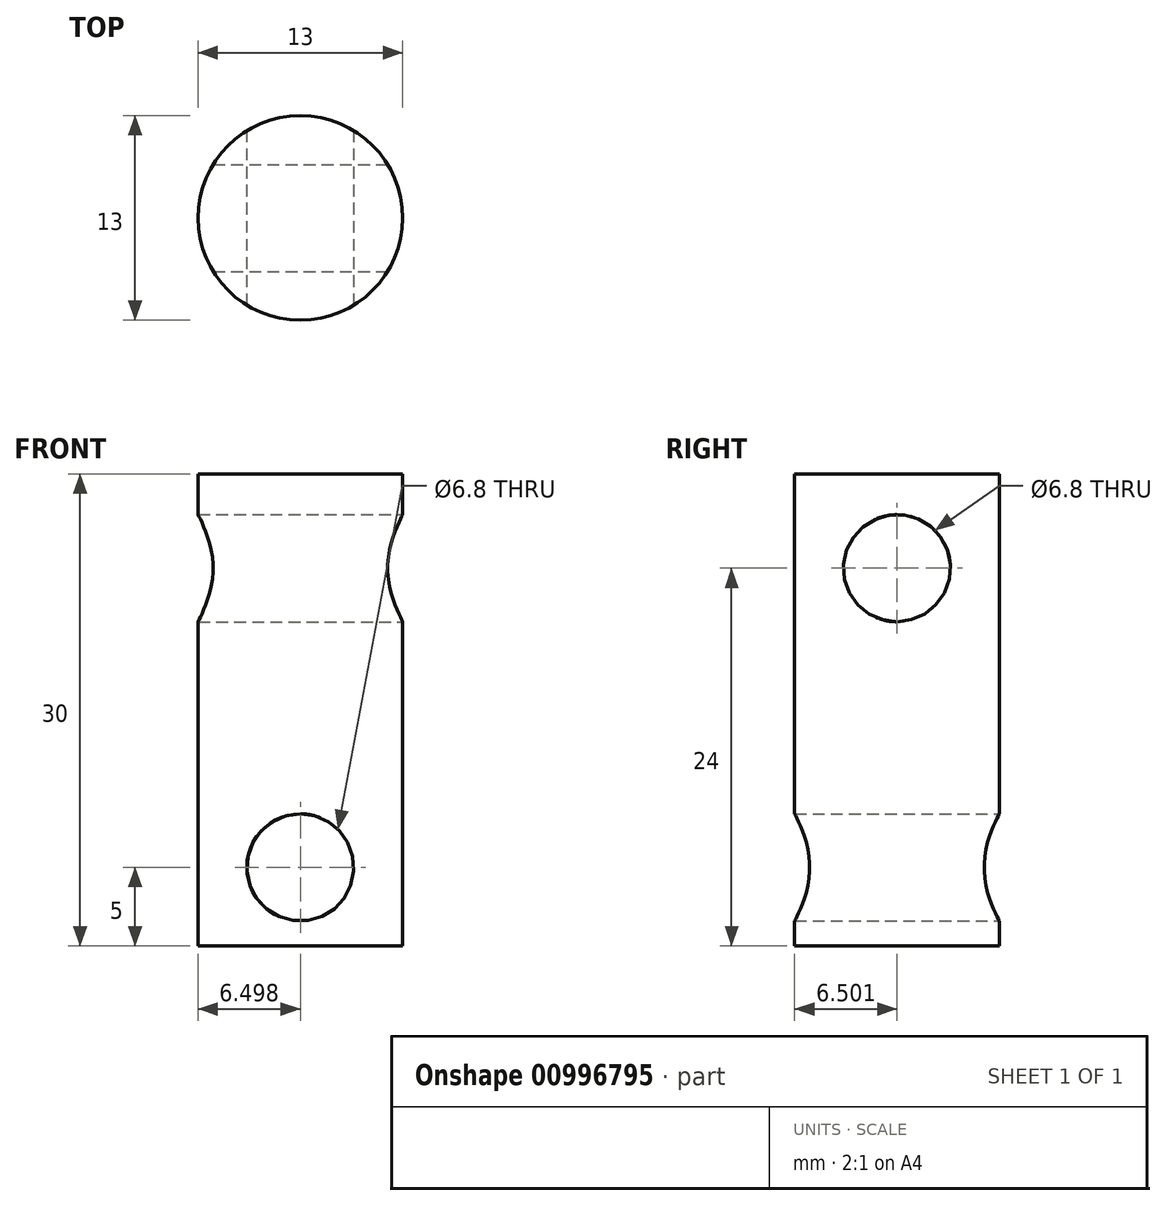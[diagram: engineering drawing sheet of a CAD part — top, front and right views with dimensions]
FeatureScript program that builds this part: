
annotation { "Feature Type Name" : "Feature", "Feature Type Description" : "" }
export const myFeature = defineFeature(function(context is Context, id is Id, definition is map)
    precondition{}
    {
        {
            var Q0;
            Q0=qCreatedBy(makeId("Top.planeOp"),FACE);
            var sketch = newSketch(context, id + "F0", { "sketchPlane" : qUnion([Q0])});
            skLineSegment(sketch, "E0.bottom", {"start": v(-6.46, 7.1) * mm, "end": v(13.54, 7.1) * mm});
            skLineSegment(sketch, "E0.top", {"start": v(-6.46, -12.9) * mm, "end": v(13.54, -12.9) * mm});
            skLineSegment(sketch, "E0.left", {"start": v(-6.46, 7.1) * mm, "end": v(-6.46, -12.9) * mm});
            skLineSegment(sketch, "E0.right", {"start": v(13.54, 7.1) * mm, "end": v(13.54, -12.9) * mm});
            skSolve(sketch);
        }
        {
            var Q0;
            Q0 = qSketchRegion(id + "F0", true);
            extrude(context, id + "F1", {"entities" : qUnion([Q0]), "depth" : 30 * mm, "offsetDistance" : 25 * mm});
        }
        {
            var Q0;
            Q0=makeQuery(id+"F1.opExtrude","SWEPT_FACE",FACE,{"disambiguationData":[OSD([sQuery(id+"F0.wireOp",EDGE,"E0.bottom")])]});
            var sketch = newSketch(context, id + "F2", { "sketchPlane" : qUnion([Q0])});
            skCircle(sketch, "E1", {"center": v(-3.54, 5) * mm, "radius": 3.4 * mm});
            skPoint(sketch, "E1.centerSnap0", {"position": v(-3.54, 0) * mm});
            skSolve(sketch);
        }
        {
            var Q0;
            Q0=makeQuery(id+"F1.opExtrude","SWEPT_FACE",FACE,{"disambiguationData":[OSD([sQuery(id+"F0.wireOp",EDGE,"E0.right")])]});
            var sketch = newSketch(context, id + "F3", { "sketchPlane" : qUnion([Q0])});
            skCircle(sketch, "E2", {"center": v(-2.9, 24) * mm, "radius": 3.4 * mm});
            skPoint(sketch, "E2.centerSnap0", {"position": v(-2.9, 30) * mm});
            skSolve(sketch);
        }
        {
            var Q0;
            Q0 = qSketchRegion(id + "F3", true);
            extrude(context, id + "F4", {"entities" : qUnion([Q0]), "operationType" : NewBodyOperationType.REMOVE, "oppositeDirection" : true, "depth" : 25 * mm, "offsetDistance" : 25 * mm});
        }
        {
            var Q0;
            Q0 = qSketchRegion(id + "F2", true);
            extrude(context, id + "F5", {"entities" : qUnion([Q0]), "operationType" : NewBodyOperationType.REMOVE, "oppositeDirection" : true, "depth" : 25 * mm, "offsetDistance" : 25 * mm});
        }
        {
            var Q0;
            Q0=makeQuery(id+"F1.opExtrude","CAP_FACE",FACE,{"disambiguationData":[OSD([sQuery(id+"F0.wireOp",EDGE,"E0.bottom"),sQuery(id+"F0.wireOp",EDGE,"E0.top"),sQuery(id+"F0.wireOp",EDGE,"E0.left"),sQuery(id+"F0.wireOp",EDGE,"E0.right")])],"isStart":true});
            var sketch = newSketch(context, id + "F6", { "sketchPlane" : qUnion([Q0])});
            skCircle(sketch, "E3", {"center": v(3.54, 2.9) * mm, "radius": 6.5 * mm});
            skPoint(sketch, "E3.centerSnap0", {"position": v(13.54, 2.9) * mm});
            skPoint(sketch, "E3.centerSnap1", {"position": v(3.54, 12.9) * mm});
            skSolve(sketch);
        }
        {
            var Q0;
            Q0=makeQuery(id+"F6.imprint","IMPRINT",FACE,{"disambiguationData":[TD([[makeQuery(id+"F6.imprint","IMPRINT",EDGE,{"derivedFrom":sQuery(id+"F6.wireOp",EDGE,"E3")}),-1.0]])]});
            extrude(context, id + "F7", {"entities" : qUnion([Q0]), "operationType" : NewBodyOperationType.REMOVE, "oppositeDirection" : true, "depth" : 30 * mm, "offsetDistance" : 25 * mm});
        }
    });
